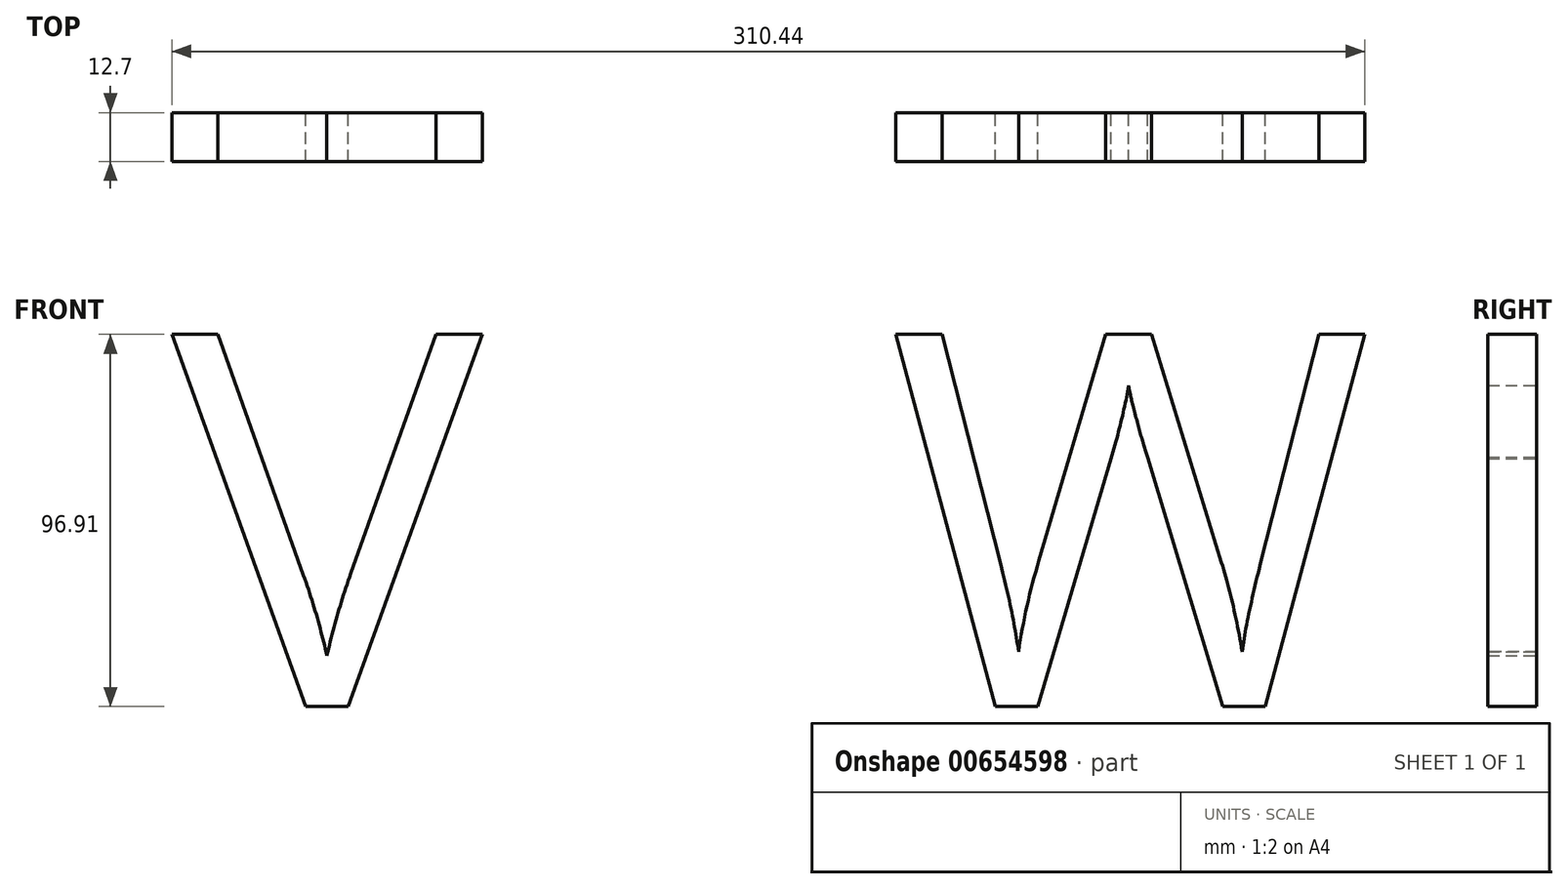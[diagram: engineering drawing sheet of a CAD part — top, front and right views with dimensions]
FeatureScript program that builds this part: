
annotation { "Feature Type Name" : "Feature", "Feature Type Description" : "" }
export const myFeature = defineFeature(function(context is Context, id is Id, definition is map)
    precondition{}
    {
        {
            var Q0;
            Q0=qCreatedBy(makeId("Front.planeOp"),FACE);
            var sketch = newSketch(context, id + "F0", { "sketchPlane" : qUnion([Q0])});
            skText(sketch, "E0", { "text": "V   W", "fontName": "OpenSans-Regular.ttf"});
            const initialGuessF0  = {"E0": [-0.05741, -0.05624, 1, 0, 0.09774]};
            skSetInitialGuess(sketch, initialGuessF0);
            skSolve(sketch);
        }
        {
            var Q0;
            Q0 = qSketchRegion(id + "F0", true);
            extrude(context, id + "F1", {"entities" : qUnion([Q0]), "depth" : 12.7 * mm, "offsetDistance" : 25.4 * mm});
        }
    });
